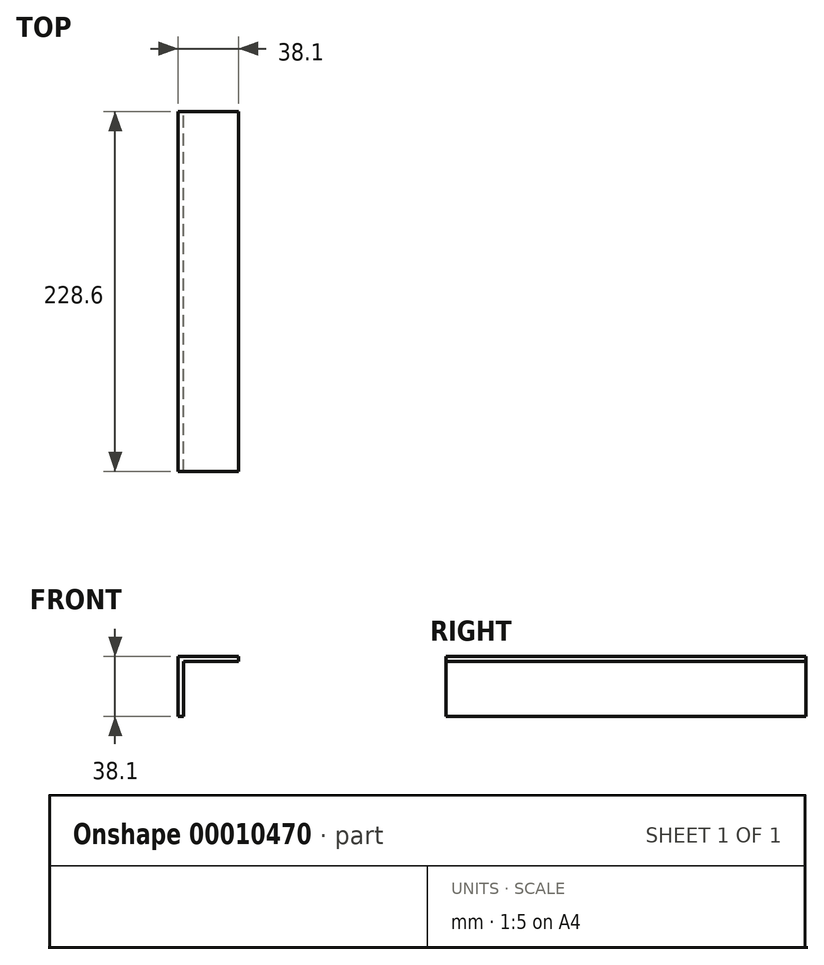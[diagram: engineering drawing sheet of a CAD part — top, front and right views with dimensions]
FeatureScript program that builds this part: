
annotation { "Feature Type Name" : "Feature", "Feature Type Description" : "" }
export const myFeature = defineFeature(function(context is Context, id is Id, definition is map)
    precondition{}
    {
        {
            var Q0;
            Q0=qCreatedBy(makeId("Front.planeOp"),FACE);
            var sketch = newSketch(context, id + "F0", { "sketchPlane" : qUnion([Q0])});
            skLineSegment(sketch, "E0", {"start": v(0, 0) * mm, "end": v(0, -34.93) * mm});
            skLineSegment(sketch, "E1", {"start": v(0, 0) * mm, "end": v(34.92, 0) * mm});
            skLineSegment(sketch, "E2.0", {"start": v(-3.18, 3.17) * mm, "end": v(-3.17, -34.93) * mm});
            skLineSegment(sketch, "E2.1", {"start": v(-3.18, 3.18) * mm, "end": v(34.92, 3.18) * mm});
            skLineSegment(sketch, "E3", {"start": v(-3.17, -34.93) * mm, "end": v(0, -34.93) * mm});
            skLineSegment(sketch, "E4", {"start": v(34.92, 0) * mm, "end": v(34.92, 3.18) * mm});
            skSolve(sketch);
        }
        {
            var Q0;
            Q0 = qSketchRegion(id + "F0", true);
            extrude(context, id + "F1", {"entities" : qUnion([Q0]), "depth" : 228.6 * mm});
        }
    });
